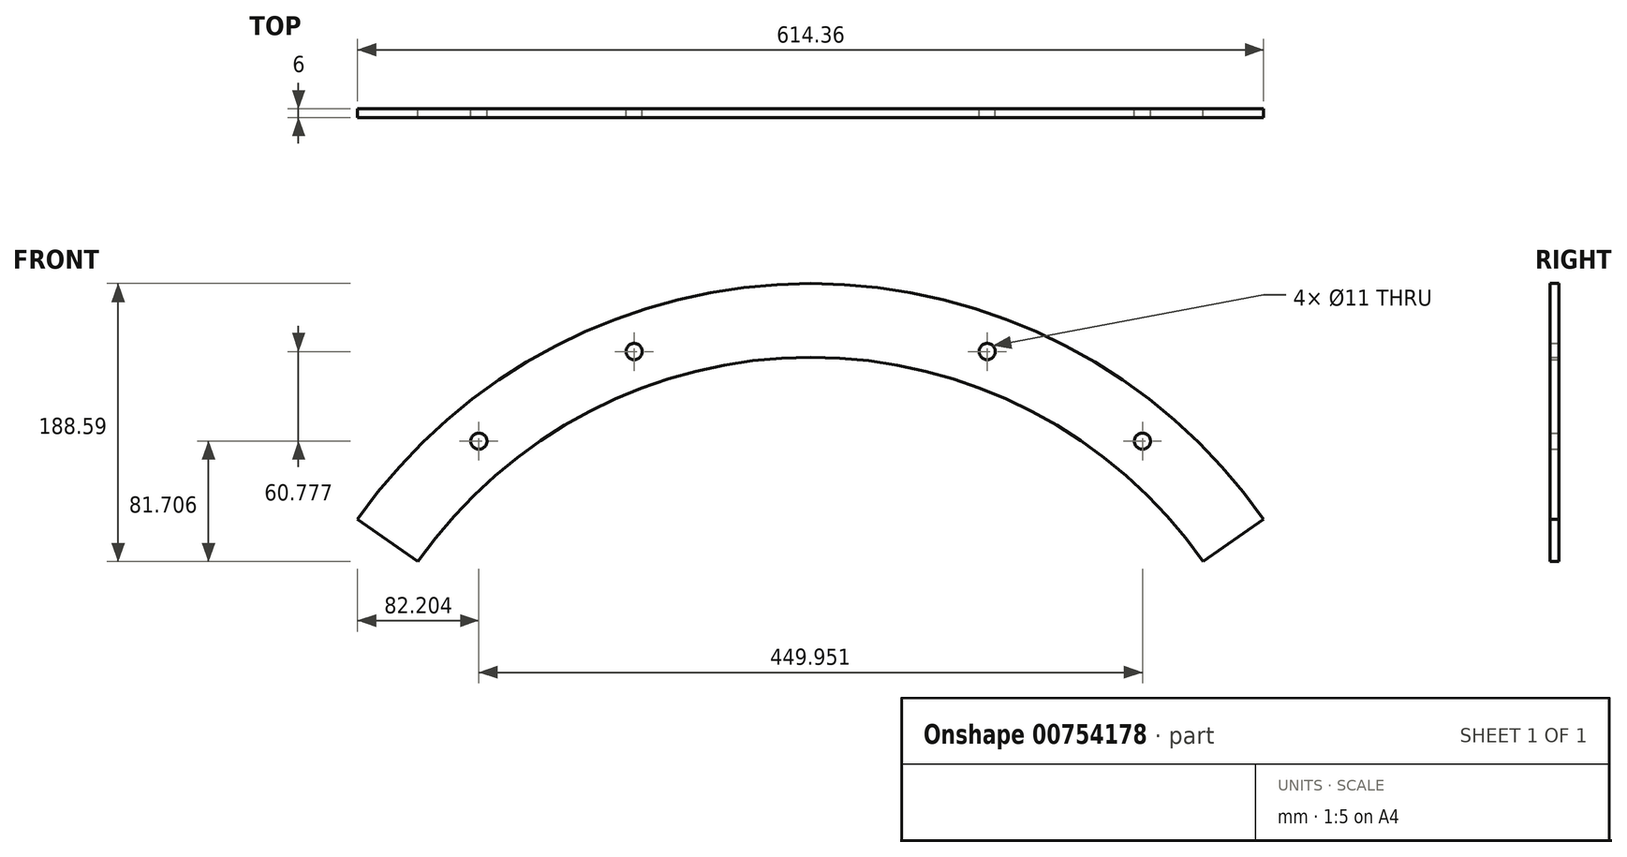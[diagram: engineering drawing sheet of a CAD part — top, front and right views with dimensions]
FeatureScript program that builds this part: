
annotation { "Feature Type Name" : "Feature", "Feature Type Description" : "" }
export const myFeature = defineFeature(function(context is Context, id is Id, definition is map)
    precondition{}
    {
        {
            var Q0;
            Q0=qCreatedBy(makeId("Front.planeOp"),FACE);
            var sketch = newSketch(context, id + "F0", { "sketchPlane" : qUnion([Q0])});
            skArc(sketch, "E0", {"start": v(307.18, 215.1) * mm, "mid": v(0, 375) * mm, "end": v(-307.18, 215.1) * mm});
            skArc(sketch, "E1", {"start": v(266.22, 186.41) * mm, "mid": v(0, 325) * mm, "end": v(-266.22, 186.41) * mm});
            skArc(sketch, "E2", {"start": v(286.7, 200.75) * mm, "mid": v(0, 350) * mm, "end": v(-286.7, 200.75) * mm, "construction": true});
            skLineSegment(sketch, "E3", {"start": v(-266.22, 186.41) * mm, "end": v(-307.18, 215.1) * mm});
            skLineSegment(sketch, "E4", {"start": v(-714.07, 500) * mm, "end": v(714.07, 500) * mm, "construction": true});
            skLineSegment(sketch, "E5", {"start": v(307.18, 215.1) * mm, "end": v(266.22, 186.41) * mm});
            skLineSegment(sketch, "E6", {"start": v(0, 0) * mm, "end": v(-543.8, 0) * mm, "construction": true});
            skLineSegment(sketch, "E7", {"start": v(0, 0) * mm, "end": v(0, 635.17) * mm, "construction": true});
            skPoint(sketch, "E7.endSnap0", {"position": v(0, 500) * mm});
            skLineSegment(sketch, "E8", {"start": v(0, 0) * mm, "end": v(-314.58, 374.9) * mm, "construction": true});
            skPoint(sketch, "E9", {"position": v(-224.98, 268.12) * mm});
            skLineSegment(sketch, "E10", {"start": v(0, 0) * mm, "end": v(-154.6, 424.74) * mm, "construction": true});
            skPoint(sketch, "E11", {"position": v(-119.7, 328.9) * mm});
            skLineSegment(sketch, "E12", {"start": v(0, 0) * mm, "end": v(824.44, 0) * mm, "construction": true});
            skLineSegment(sketch, "E13.MirrorCS", {"start": v(0, 0) * mm, "end": v(314.58, 374.9) * mm, "construction": true});
            skLineSegment(sketch, "E14.MirrorCS", {"start": v(0, 0) * mm, "end": v(154.6, 424.74) * mm, "construction": true});
            skPoint(sketch, "E15.MirrorP", {"position": v(224.98, 268.12) * mm});
            skPoint(sketch, "E16.MirrorP", {"position": v(119.7, 328.9) * mm});
            skSolve(sketch);
        }
        {
            var Q0;
            Q0 = qSketchRegion(id + "F0", true);
            extrude(context, id + "F1", {"entities" : qUnion([Q0]), "depth" : 6 * mm, "offsetDistance" : 25 * mm});
        }
        {
            var Q0;
            Q0=sQuery(id+"F0.wireOp",VERTEX,"E9");
            var Q1;
            Q1=sQuery(id+"F0.wireOp",VERTEX,"E11");
            var Q2;
            Q2=sQuery(id+"F0.wireOp",VERTEX,"E16.MirrorP");
            var Q3;
            Q3=sQuery(id+"F0.wireOp",VERTEX,"E15.MirrorP");
            var Q4;
            Q4=makeQuery(id+"F1.opExtrude","SWEPT_BODY",BODY,{"disambiguationData":[OSD([sQuery(id+"F0.wireOp",EDGE,"E0"),sQuery(id+"F0.wireOp",EDGE,"E1"),sQuery(id+"F0.wireOp",EDGE,"E3"),sQuery(id+"F0.wireOp",EDGE,"E5")])]});
            hole(context, id + "F2", {"style" : HoleStyle.SIMPLE, "endStyle" : HoleEndStyle.THROUGH, "oppositeDirection" : true, "standardTappedOrClearance" : lookupTablePath({ "standard" : "ISO", "fit" : "Normal", "size" : "M10", "type" : "Clearance" }), "standardBlindInLast" : lookupTablePath({ "fit" : "Standard", "standard" : "ISO", "size" : "M10", "type" : "Clearance" }), "holeDiameter" : 11 * mm, "majorDiameter" : 5 * mm, "isTappedThrough" : true, "tappedDepth" : 12 * mm, "tapClearance" : 3, "locations" : qUnion([Q0, Q1, Q2, Q3]), "scope" : qUnion([Q4])});
        }
    });
